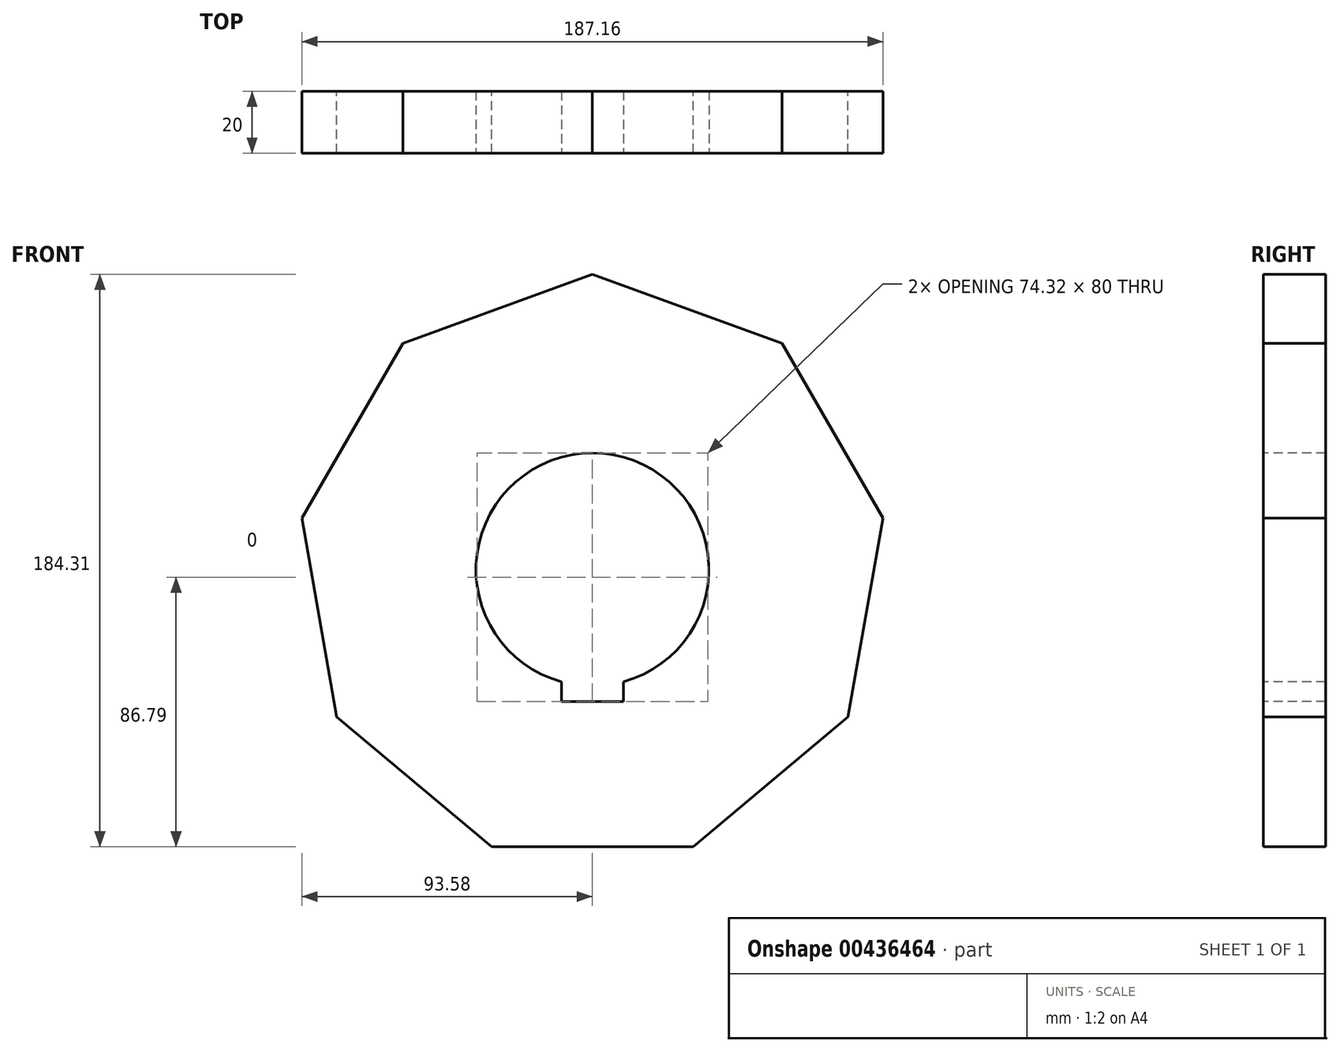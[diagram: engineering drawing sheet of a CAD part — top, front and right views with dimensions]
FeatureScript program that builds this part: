
annotation { "Feature Type Name" : "Feature", "Feature Type Description" : "" }
export const myFeature = defineFeature(function(context is Context, id is Id, definition is map)
    precondition{}
    {
        {
            var Q0;
            Q0=qCreatedBy(makeId("Front.planeOp"),FACE);
            var sketch = newSketch(context, id + "F0", { "sketchPlane" : qUnion([Q0])});
            skCircle(sketch, "E0.cCircle", {"center": v(0, 0) * mm, "radius": 95.02 * mm, "construction": true});
            skLineSegment(sketch, "E0.0", {"start": v(32.5, -89.3) * mm, "end": v(-32.5, -89.3) * mm});
            skLineSegment(sketch, "E0.1", {"start": v(-32.5, -89.3) * mm, "end": v(-82.3, -47.51) * mm});
            skLineSegment(sketch, "E0.2", {"start": v(-82.3, -47.51) * mm, "end": v(-93.58, 16.5) * mm});
            skLineSegment(sketch, "E0.3", {"start": v(-93.58, 16.5) * mm, "end": v(-61.08, 72.8) * mm});
            skLineSegment(sketch, "E0.4", {"start": v(-61.08, 72.8) * mm, "end": v(0, 95.02) * mm});
            skLineSegment(sketch, "E0.5", {"start": v(0, 95.02) * mm, "end": v(61.08, 72.8) * mm});
            skLineSegment(sketch, "E0.6", {"start": v(61.08, 72.8) * mm, "end": v(93.58, 16.5) * mm});
            skLineSegment(sketch, "E0.7", {"start": v(93.58, 16.5) * mm, "end": v(82.3, -47.51) * mm});
            skLineSegment(sketch, "E0.8", {"start": v(82.3, -47.51) * mm, "end": v(32.5, -89.3) * mm});
            skSolve(sketch);
        }
        {
            var Q0;
            Q0 = qSketchRegion(id + "F0", true);
            extrude(context, id + "F1", {"entities" : qUnion([Q0]), "depth" : 20 * mm});
        }
        {
            var Q0;
            Q0=makeQuery(id+"F1.opExtrude","CAP_FACE",FACE,{"disambiguationData":[OSD([sQuery(id+"F0.wireOp",EDGE,"E0.0"),sQuery(id+"F0.wireOp",EDGE,"E0.1"),sQuery(id+"F0.wireOp",EDGE,"E0.2"),sQuery(id+"F0.wireOp",EDGE,"E0.3"),sQuery(id+"F0.wireOp",EDGE,"E0.4"),sQuery(id+"F0.wireOp",EDGE,"E0.5"),sQuery(id+"F0.wireOp",EDGE,"E0.6"),sQuery(id+"F0.wireOp",EDGE,"E0.7"),sQuery(id+"F0.wireOp",EDGE,"E0.8")])],"isStart":false});
            var sketch = newSketch(context, id + "F2", { "sketchPlane" : qUnion([Q0])});
            skArc(sketch, "E1", {"start": v(10, -36.14) * mm, "mid": v(0, 37.5) * mm, "end": v(-10, -36.14) * mm});
            skLineSegment(sketch, "E2", {"start": v(0, -42.5) * mm, "end": v(-10, -42.5) * mm});
            skLineSegment(sketch, "E3", {"start": v(0, -42.5) * mm, "end": v(10, -42.5) * mm});
            skLineSegment(sketch, "E4", {"start": v(10, -42.5) * mm, "end": v(10, -36.14) * mm});
            skLineSegment(sketch, "E5", {"start": v(-10, -42.5) * mm, "end": v(-10, -36.14) * mm});
            skPoint(sketch, "E6.start.orphan", {"position": v(0, -37.5) * mm});
            skSolve(sketch);
        }
        {
            var Q0;
            Q0 = qSketchRegion(id + "F2", true);
            var Q1;
            Q1=makeQuery(id+"F2.imprint","IMPRINT",FACE,{"disambiguationData":[TD([[makeQuery(id+"F2.imprint","IMPRINT",EDGE,{"derivedFrom":sQuery(id+"F2.wireOp",EDGE,"E1")}),1.0]])]});
            extrude(context, id + "F3", {"entities" : qUnion([Q0, Q1]), "operationType" : NewBodyOperationType.REMOVE, "oppositeDirection" : true, "depth" : 25 * mm});
        }
    });
